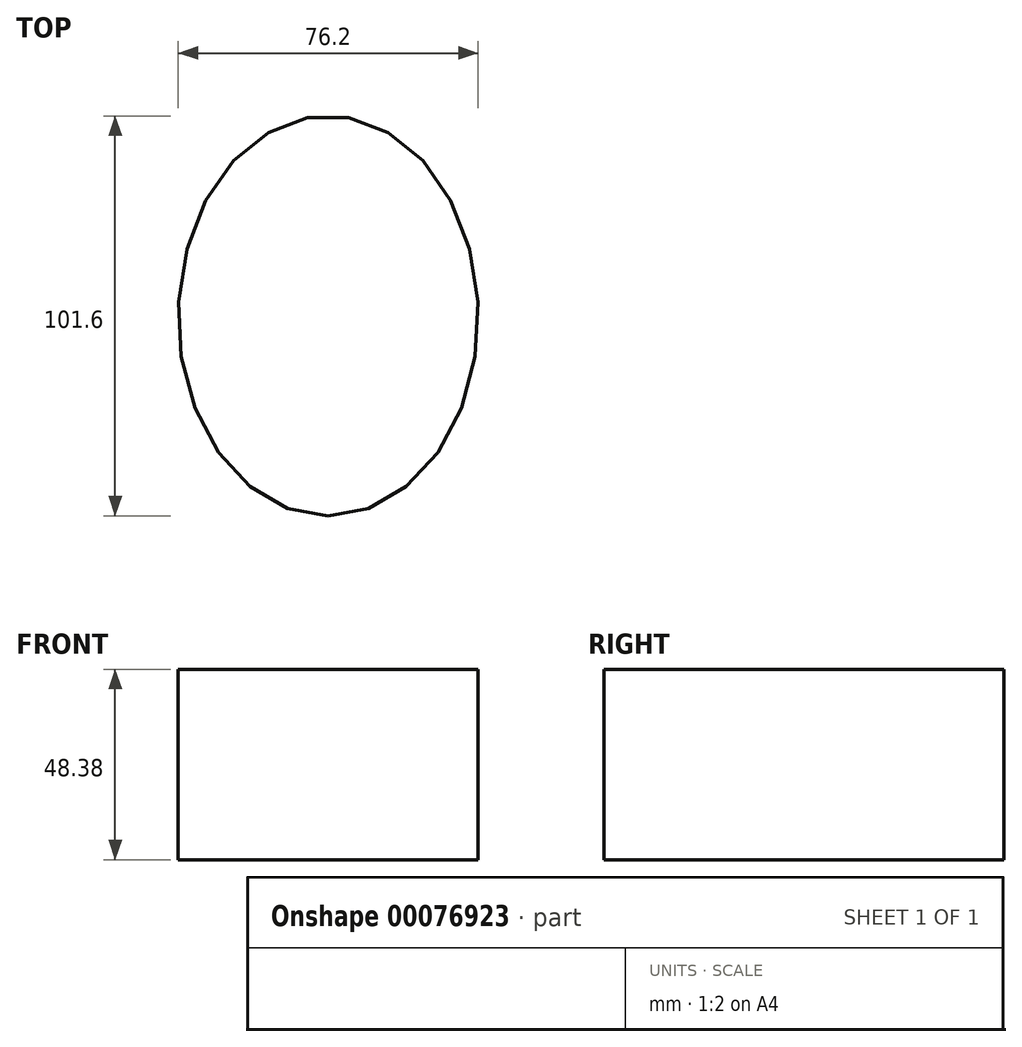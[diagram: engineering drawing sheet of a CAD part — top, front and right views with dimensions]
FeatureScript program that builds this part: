
annotation { "Feature Type Name" : "Feature", "Feature Type Description" : "" }
export const myFeature = defineFeature(function(context is Context, id is Id, definition is map)
    precondition{}
    {
        {
            var Q0;
            Q0=qCreatedBy(makeId("Top.planeOp"),FACE);
            var sketch = newSketch(context, id + "F0", { "sketchPlane" : qUnion([Q0])});
            skEllipse(sketch, "E0", {"center": v(0, 0) * mm, "majorRadius": 50.8 * mm, "minorRadius": 38.1 * mm, "majorAxis": v(0, -1)});
            skSolve(sketch);
        }
        {
            var Q0;
            Q0=makeQuery(id+"F0.imprint","IMPRINT",FACE,{"disambiguationData":[TD([[makeQuery(id+"F0.imprint","IMPRINT",EDGE,{"derivedFrom":sQuery(id+"F0.wireOp",EDGE,"E0")}),1.0]])]});
            extrude(context, id + "F1", {"entities" : qUnion([Q0]), "depth" : 48.38 * mm});
        }
    });
